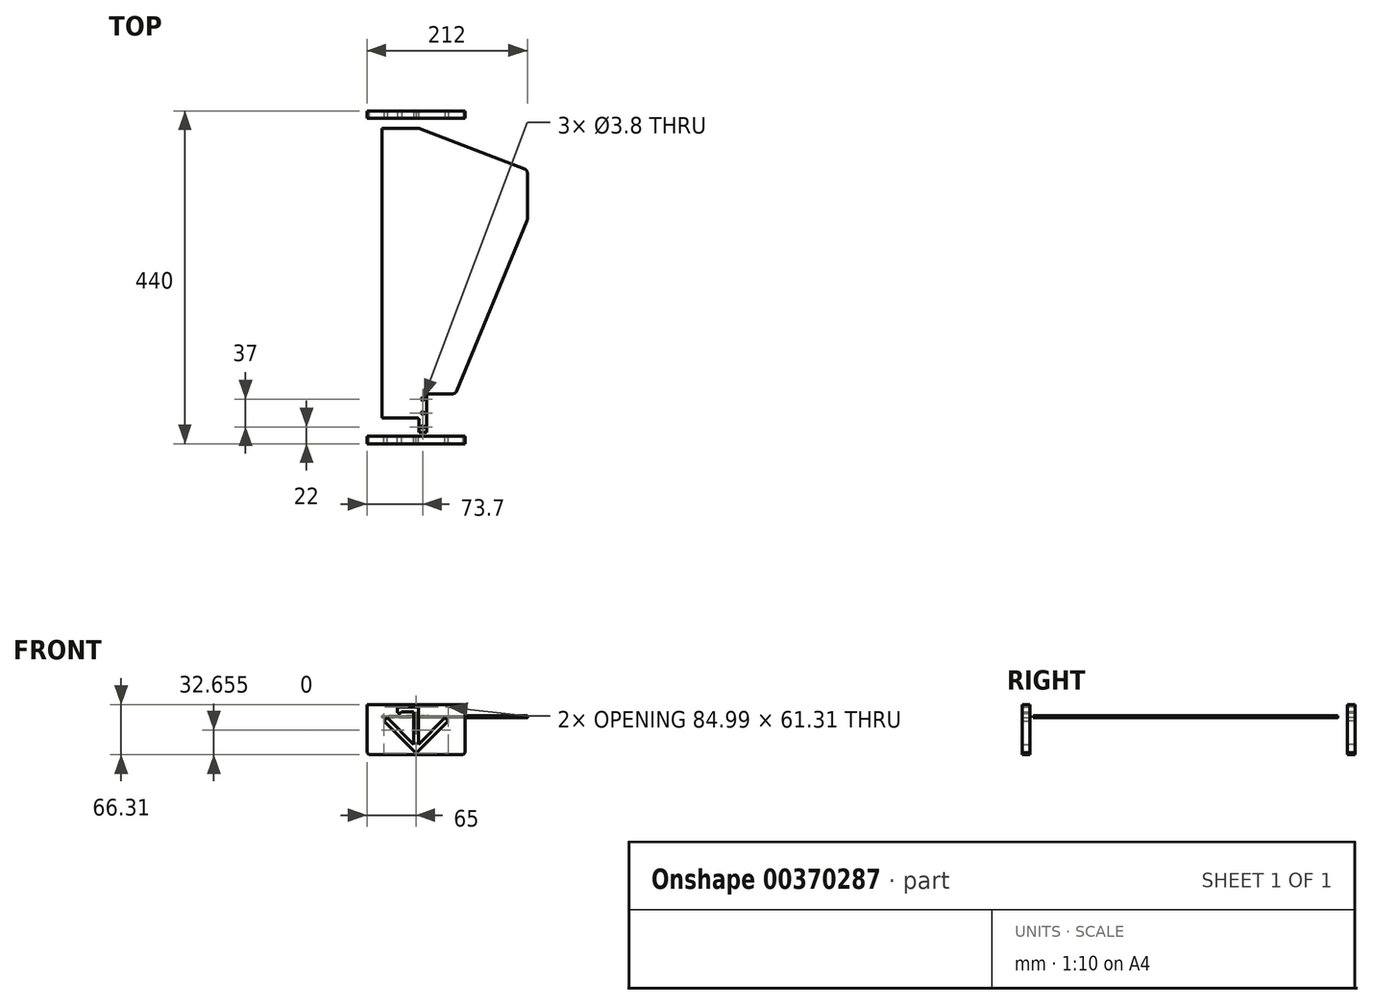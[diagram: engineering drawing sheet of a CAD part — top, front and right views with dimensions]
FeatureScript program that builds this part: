
annotation { "Feature Type Name" : "Feature", "Feature Type Description" : "" }
export const myFeature = defineFeature(function(context is Context, id is Id, definition is map)
    precondition{}
    {
        {
            var Q0;
            Q0=qCreatedBy(makeId("Top.planeOp"),FACE);
            var sketch = newSketch(context, id + "F0", { "sketchPlane" : qUnion([Q0])});
            skLineSegment(sketch, "E0", {"start": v(53.19, 59.09) * mm, "end": v(146.62, 284.65) * mm});
            skLineSegment(sketch, "E1", {"start": v(3.8, 406.67) * mm, "end": v(143.8, 352.93) * mm});
            skLineSegment(sketch, "E2", {"start": v(13.7, 5) * mm, "end": v(13.7, 53) * mm});
            skLineSegment(sketch, "E3", {"start": v(16.7, 56) * mm, "end": v(48.57, 56) * mm});
            skLineSegment(sketch, "E4", {"start": v(4, 5) * mm, "end": v(13.7, 5) * mm});
            skLineSegment(sketch, "E5", {"start": v(147, 348.26) * mm, "end": v(147, 286.57) * mm});
            skArc(sketch, "E6.filletArc", {"start": v(3.8, 406.67) * mm, "mid": v(2.91, 406.92) * mm, "end": v(2, 407) * mm});
            skPoint(sketch, "E7.visualSharp", {"position": v(147, 351.7) * mm});
            skArc(sketch, "E7.filletArc", {"start": v(147, 348.26) * mm, "mid": v(146.12, 351.1) * mm, "end": v(143.8, 352.93) * mm});
            skPoint(sketch, "E8.visualSharp", {"position": v(147, 285.57) * mm});
            skArc(sketch, "E8.filletArc", {"start": v(146.62, 284.65) * mm, "mid": v(146.9, 285.6) * mm, "end": v(147, 286.57) * mm});
            skPoint(sketch, "E9.visualSharp", {"position": v(51.9, 56) * mm});
            skArc(sketch, "E9.filletArc", {"start": v(48.57, 56) * mm, "mid": v(51.35, 56.84) * mm, "end": v(53.19, 59.09) * mm});
            skArc(sketch, "E10.filletArc", {"start": v(16.7, 56) * mm, "mid": v(14.58, 55.12) * mm, "end": v(13.7, 53) * mm});
            skCircle(sketch, "E11", {"center": v(8.7, 12) * mm, "radius": 1.9 * mm});
            skCircle(sketch, "E12", {"center": v(8.7, 49) * mm, "radius": 1.9 * mm});
            skLineSegment(sketch, "E13.0", {"start": v(8.7, 12) * mm, "end": v(8.7, 49) * mm, "construction": true});
            skCircle(sketch, "E14", {"center": v(8.7, 30.5) * mm, "radius": 1.9 * mm});
            skLineSegment(sketch, "E15", {"start": v(2, 407) * mm, "end": v(-45, 407) * mm});
            skLineSegment(sketch, "E16", {"start": v(-45, 407) * mm, "end": v(-45, 24) * mm});
            skLineSegment(sketch, "E17", {"start": v(-45, 24) * mm, "end": v(1, 24) * mm});
            skLineSegment(sketch, "E18", {"start": v(4, 21) * mm, "end": v(4, 5) * mm});
            skPoint(sketch, "E19.visualSharp", {"position": v(4, 24) * mm});
            skArc(sketch, "E19.filletArc", {"start": v(4, 21) * mm, "mid": v(3.12, 23.12) * mm, "end": v(1, 24) * mm});
            skPoint(sketch, "E20", {"position": v(0, 0) * mm});
            skSolve(sketch);
        }
        {
            var Q0;
            Q0=qCreatedBy(makeId("Front.planeOp"),FACE);
            var sketch = newSketch(context, id + "F1", { "sketchPlane" : qUnion([Q0])});
            skPoint(sketch, "E21", {"position": v(-38.18, -3) * mm});
            skLineSegment(sketch, "E22", {"start": v(-65, -51.81) * mm, "end": v(62, -51.81) * mm});
            skLineSegment(sketch, "E23", {"start": v(3.05, -38.13) * mm, "end": v(38.18, -3) * mm});
            skLineSegment(sketch, "E24", {"start": v(38.18, -3) * mm, "end": v(42.5, -7.31) * mm});
            skLineSegment(sketch, "E25", {"start": v(42.5, -7.31) * mm, "end": v(0, -49.81) * mm});
            skLineSegment(sketch, "E26", {"start": v(0, -49.81) * mm, "end": v(-42.5, -7.31) * mm});
            skLineSegment(sketch, "E27", {"start": v(-42.5, -7.31) * mm, "end": v(-38.18, -3) * mm});
            skLineSegment(sketch, "E28", {"start": v(-38.18, -3) * mm, "end": v(-3.05, -38.13) * mm});
            skPoint(sketch, "E29", {"position": v(0, -51.81) * mm});
            skLineSegment(sketch, "E30.direction1", {"start": v(-65, -51.81) * mm, "end": v(0, -51.81) * mm, "construction": true});
            skLineSegment(sketch, "E31", {"start": v(62, -51.81) * mm, "end": v(65, -48.81) * mm});
            skPoint(sketch, "E32.orphan", {"position": v(65, -51.81) * mm});
            skLineSegment(sketch, "E33", {"start": v(-62, -51.81) * mm, "end": v(-65, -48.81) * mm});
            skLineSegment(sketch, "E34", {"start": v(-7.92, 197.19) * mm, "end": v(-41.42, 197.19) * mm});
            skLineSegment(sketch, "E35", {"start": v(-44.42, 194.19) * mm, "end": v(-41.42, 197.19) * mm});
            skLineSegment(sketch, "E36", {"start": v(-7.92, 197.19) * mm, "end": v(-4.92, 194.19) * mm});
            skLineSegment(sketch, "E37", {"start": v(5.5, 194.19) * mm, "end": v(8.5, 197.19) * mm});
            skPoint(sketch, "E38.orphan", {"position": v(-4.92, 197.19) * mm});
            skPoint(sketch, "E39.orphan", {"position": v(6.08, 197.19) * mm});
            skLineSegment(sketch, "E40", {"start": v(-3.05, -38.13) * mm, "end": v(-3.05, 4.5) * mm});
            skLineSegment(sketch, "E41", {"start": v(3.05, -38.13) * mm, "end": v(3.05, 5) * mm});
            skPoint(sketch, "E42", {"position": v(38.18, -3) * mm});
            skPoint(sketch, "E43", {"position": v(38.18, 0) * mm});
            skCircle(sketch, "E44", {"center": v(0, 3) * mm, "radius": 3 * mm});
            skLineSegment(sketch, "E45", {"start": v(-3.55, 5) * mm, "end": v(-19.28, 5) * mm});
            skArc(sketch, "E46", {"start": v(-25.11, 6) * mm, "mid": v(-22.62, 3.04) * mm, "end": v(-19.28, 5) * mm});
            skLineSegment(sketch, "E47", {"start": v(-25.11, 11.5) * mm, "end": v(3.05, 11.5) * mm});
            skLineSegment(sketch, "E48", {"start": v(-25.11, 11.5) * mm, "end": v(-25.11, 6) * mm});
            skLineSegment(sketch, "E49", {"start": v(-3.55, 5) * mm, "end": v(-3.05, 4.5) * mm});
            skLineSegment(sketch, "E50", {"start": v(3.05, 5) * mm, "end": v(3.05, 11.5) * mm});
            skPoint(sketch, "E51.orphan", {"position": v(-3.05, 5) * mm});
            skLineSegment(sketch, "E52", {"start": v(-65, -48.81) * mm, "end": v(-65, 14.5) * mm});
            skLineSegment(sketch, "E53", {"start": v(-65, 14.5) * mm, "end": v(65, 14.5) * mm});
            skLineSegment(sketch, "E54", {"start": v(65, 14.5) * mm, "end": v(65, -48.81) * mm});
            skPoint(sketch, "E55", {"position": v(-29, -7.95) * mm});
            skSolve(sketch);
        }
        {
            var Q0;
            Q0=qSketchRegion(id+"F1",true);
            extrude(context, id + "F2", {"entities" : qUnion([Q0]), "depth" : 10 * mm});
        }
        {
            var Q0;
            Q0=qCreatedBy(makeId("Front.planeOp"),FACE);
            cPlane(context, id + "F3", {"entities" : qUnion([Q0]), "cplaneType" : CPlaneType.OFFSET, "offset" : 210 * mm, "oppositeDirection" : true, "width" : 150 * mm, "height" : 150 * mm});
        }
        {
            var Q0;
            Q0=makeQuery(id+"F2.opExtrude","SWEPT_BODY",BODY,{"disambiguationData":[OSD([sQuery(id+"F1.wireOp",EDGE,"E22"),sQuery(id+"F1.wireOp",EDGE,"1cbbb176-f40a-4f1c-aaf5-e4b3a7756a65"),sQuery(id+"F1.wireOp",EDGE,"0db14ab7-eb58-4049-9c12-30ca4f5b9e90"),sQuery(id+"F1.wireOp",EDGE,"ab1c63a4-a027-4243-88f4-a372497609cb"),sQuery(id+"F1.wireOp",EDGE,"E23"),sQuery(id+"F1.wireOp",EDGE,"E24"),sQuery(id+"F1.wireOp",EDGE,"E25"),sQuery(id+"F1.wireOp",EDGE,"E26"),sQuery(id+"F1.wireOp",EDGE,"E27"),sQuery(id+"F1.wireOp",EDGE,"E28"),sQuery(id+"F1.wireOp",EDGE,"b1abd40f-1537-4efa-8357-bc5ce063cbbe"),sQuery(id+"F1.wireOp",EDGE,"d6b29baa-6176-45ec-b0cb-b8b1ffd4a9fb"),sQuery(id+"F1.wireOp",EDGE,"2be75464-0c29-4c82-b3b4-490e88410c14"),sQuery(id+"F1.wireOp",EDGE,"684266eb-fe4b-4d2b-8d3a-21344d5b1583.0.1.0"),sQuery(id+"F1.wireOp",EDGE,"684266eb-fe4b-4d2b-8d3a-21344d5b1583.0.1.1"),sQuery(id+"F1.wireOp",EDGE,"684266eb-fe4b-4d2b-8d3a-21344d5b1583.0.1.3"),sQuery(id+"F1.wireOp",EDGE,"684266eb-fe4b-4d2b-8d3a-21344d5b1583.0.1.4"),sQuery(id+"F1.wireOp",EDGE,"684266eb-fe4b-4d2b-8d3a-21344d5b1583.0.1.5"),sQuery(id+"F1.wireOp",EDGE,"684266eb-fe4b-4d2b-8d3a-21344d5b1583.0.1.6"),sQuery(id+"F1.wireOp",EDGE,"684266eb-fe4b-4d2b-8d3a-21344d5b1583.0.1.7"),sQuery(id+"F1.wireOp",EDGE,"684266eb-fe4b-4d2b-8d3a-21344d5b1583.0.1.9"),sQuery(id+"F1.wireOp",EDGE,"684266eb-fe4b-4d2b-8d3a-21344d5b1583.0.1.10"),sQuery(id+"F1.wireOp",EDGE,"684266eb-fe4b-4d2b-8d3a-21344d5b1583.0.1.11"),sQuery(id+"F1.wireOp",EDGE,"684266eb-fe4b-4d2b-8d3a-21344d5b1583.0.1.12"),sQuery(id+"F1.wireOp",EDGE,"684266eb-fe4b-4d2b-8d3a-21344d5b1583.0.2.0"),sQuery(id+"F1.wireOp",EDGE,"684266eb-fe4b-4d2b-8d3a-21344d5b1583.0.2.1"),sQuery(id+"F1.wireOp",EDGE,"684266eb-fe4b-4d2b-8d3a-21344d5b1583.0.2.3"),sQuery(id+"F1.wireOp",EDGE,"684266eb-fe4b-4d2b-8d3a-21344d5b1583.0.2.4"),sQuery(id+"F1.wireOp",EDGE,"684266eb-fe4b-4d2b-8d3a-21344d5b1583.0.2.5"),sQuery(id+"F1.wireOp",EDGE,"684266eb-fe4b-4d2b-8d3a-21344d5b1583.0.2.6"),sQuery(id+"F1.wireOp",EDGE,"684266eb-fe4b-4d2b-8d3a-21344d5b1583.0.2.7"),sQuery(id+"F1.wireOp",EDGE,"684266eb-fe4b-4d2b-8d3a-21344d5b1583.0.2.9"),sQuery(id+"F1.wireOp",EDGE,"684266eb-fe4b-4d2b-8d3a-21344d5b1583.0.2.10"),sQuery(id+"F1.wireOp",EDGE,"684266eb-fe4b-4d2b-8d3a-21344d5b1583.0.2.11"),sQuery(id+"F1.wireOp",EDGE,"684266eb-fe4b-4d2b-8d3a-21344d5b1583.0.2.12"),sQuery(id+"F1.wireOp",EDGE,"684266eb-fe4b-4d2b-8d3a-21344d5b1583.0.3.0"),sQuery(id+"F1.wireOp",EDGE,"684266eb-fe4b-4d2b-8d3a-21344d5b1583.0.3.1"),sQuery(id+"F1.wireOp",EDGE,"684266eb-fe4b-4d2b-8d3a-21344d5b1583.0.3.3"),sQuery(id+"F1.wireOp",EDGE,"684266eb-fe4b-4d2b-8d3a-21344d5b1583.0.3.4"),sQuery(id+"F1.wireOp",EDGE,"684266eb-fe4b-4d2b-8d3a-21344d5b1583.0.3.5"),sQuery(id+"F1.wireOp",EDGE,"684266eb-fe4b-4d2b-8d3a-21344d5b1583.0.3.6"),sQuery(id+"F1.wireOp",EDGE,"684266eb-fe4b-4d2b-8d3a-21344d5b1583.0.3.7"),sQuery(id+"F1.wireOp",EDGE,"684266eb-fe4b-4d2b-8d3a-21344d5b1583.0.3.9"),sQuery(id+"F1.wireOp",EDGE,"684266eb-fe4b-4d2b-8d3a-21344d5b1583.0.3.10"),sQuery(id+"F1.wireOp",EDGE,"684266eb-fe4b-4d2b-8d3a-21344d5b1583.0.3.11"),sQuery(id+"F1.wireOp",EDGE,"684266eb-fe4b-4d2b-8d3a-21344d5b1583.0.3.12"),sQuery(id+"F1.wireOp",EDGE,"684266eb-fe4b-4d2b-8d3a-21344d5b1583.0.4.0"),sQuery(id+"F1.wireOp",EDGE,"684266eb-fe4b-4d2b-8d3a-21344d5b1583.0.4.1"),sQuery(id+"F1.wireOp",EDGE,"684266eb-fe4b-4d2b-8d3a-21344d5b1583.0.4.3"),sQuery(id+"F1.wireOp",EDGE,"684266eb-fe4b-4d2b-8d3a-21344d5b1583.0.4.4"),sQuery(id+"F1.wireOp",EDGE,"684266eb-fe4b-4d2b-8d3a-21344d5b1583.0.4.5"),sQuery(id+"F1.wireOp",EDGE,"684266eb-fe4b-4d2b-8d3a-21344d5b1583.0.4.6"),sQuery(id+"F1.wireOp",EDGE,"684266eb-fe4b-4d2b-8d3a-21344d5b1583.0.4.7"),sQuery(id+"F1.wireOp",EDGE,"684266eb-fe4b-4d2b-8d3a-21344d5b1583.0.4.9"),sQuery(id+"F1.wireOp",EDGE,"684266eb-fe4b-4d2b-8d3a-21344d5b1583.0.4.10"),sQuery(id+"F1.wireOp",EDGE,"684266eb-fe4b-4d2b-8d3a-21344d5b1583.0.4.11"),sQuery(id+"F1.wireOp",EDGE,"684266eb-fe4b-4d2b-8d3a-21344d5b1583.0.4.12"),sQuery(id+"F1.wireOp",EDGE,"684266eb-fe4b-4d2b-8d3a-21344d5b1583.0.5.0"),sQuery(id+"F1.wireOp",EDGE,"684266eb-fe4b-4d2b-8d3a-21344d5b1583.0.5.1"),sQuery(id+"F1.wireOp",EDGE,"684266eb-fe4b-4d2b-8d3a-21344d5b1583.0.5.3"),sQuery(id+"F1.wireOp",EDGE,"684266eb-fe4b-4d2b-8d3a-21344d5b1583.0.5.4"),sQuery(id+"F1.wireOp",EDGE,"684266eb-fe4b-4d2b-8d3a-21344d5b1583.0.5.5"),sQuery(id+"F1.wireOp",EDGE,"684266eb-fe4b-4d2b-8d3a-21344d5b1583.0.5.6"),sQuery(id+"F1.wireOp",EDGE,"684266eb-fe4b-4d2b-8d3a-21344d5b1583.0.5.7"),sQuery(id+"F1.wireOp",EDGE,"684266eb-fe4b-4d2b-8d3a-21344d5b1583.0.5.9"),sQuery(id+"F1.wireOp",EDGE,"684266eb-fe4b-4d2b-8d3a-21344d5b1583.0.5.10"),sQuery(id+"F1.wireOp",EDGE,"684266eb-fe4b-4d2b-8d3a-21344d5b1583.0.5.11"),sQuery(id+"F1.wireOp",EDGE,"684266eb-fe4b-4d2b-8d3a-21344d5b1583.0.5.12"),sQuery(id+"F1.wireOp",EDGE,"684266eb-fe4b-4d2b-8d3a-21344d5b1583.0.6.0"),sQuery(id+"F1.wireOp",EDGE,"684266eb-fe4b-4d2b-8d3a-21344d5b1583.0.6.1"),sQuery(id+"F1.wireOp",EDGE,"684266eb-fe4b-4d2b-8d3a-21344d5b1583.0.6.3"),sQuery(id+"F1.wireOp",EDGE,"684266eb-fe4b-4d2b-8d3a-21344d5b1583.0.6.4"),sQuery(id+"F1.wireOp",EDGE,"684266eb-fe4b-4d2b-8d3a-21344d5b1583.0.6.5"),sQuery(id+"F1.wireOp",EDGE,"684266eb-fe4b-4d2b-8d3a-21344d5b1583.0.6.6"),sQuery(id+"F1.wireOp",EDGE,"684266eb-fe4b-4d2b-8d3a-21344d5b1583.0.6.7"),sQuery(id+"F1.wireOp",EDGE,"684266eb-fe4b-4d2b-8d3a-21344d5b1583.0.6.9"),sQuery(id+"F1.wireOp",EDGE,"684266eb-fe4b-4d2b-8d3a-21344d5b1583.0.6.10"),sQuery(id+"F1.wireOp",EDGE,"684266eb-fe4b-4d2b-8d3a-21344d5b1583.0.6.11"),sQuery(id+"F1.wireOp",EDGE,"684266eb-fe4b-4d2b-8d3a-21344d5b1583.0.6.12"),sQuery(id+"F1.wireOp",EDGE,"684266eb-fe4b-4d2b-8d3a-21344d5b1583.0.7.0"),sQuery(id+"F1.wireOp",EDGE,"684266eb-fe4b-4d2b-8d3a-21344d5b1583.0.7.1"),sQuery(id+"F1.wireOp",EDGE,"684266eb-fe4b-4d2b-8d3a-21344d5b1583.0.7.3"),sQuery(id+"F1.wireOp",EDGE,"684266eb-fe4b-4d2b-8d3a-21344d5b1583.0.7.4"),sQuery(id+"F1.wireOp",EDGE,"684266eb-fe4b-4d2b-8d3a-21344d5b1583.0.7.5"),sQuery(id+"F1.wireOp",EDGE,"684266eb-fe4b-4d2b-8d3a-21344d5b1583.0.7.6"),sQuery(id+"F1.wireOp",EDGE,"684266eb-fe4b-4d2b-8d3a-21344d5b1583.0.7.7"),sQuery(id+"F1.wireOp",EDGE,"684266eb-fe4b-4d2b-8d3a-21344d5b1583.0.7.9"),sQuery(id+"F1.wireOp",EDGE,"684266eb-fe4b-4d2b-8d3a-21344d5b1583.0.7.10"),sQuery(id+"F1.wireOp",EDGE,"684266eb-fe4b-4d2b-8d3a-21344d5b1583.0.7.11"),sQuery(id+"F1.wireOp",EDGE,"684266eb-fe4b-4d2b-8d3a-21344d5b1583.0.7.12"),sQuery(id+"F1.wireOp",EDGE,"5e48dbf6-bd7d-4e66-b090-3bfb0b5fe9680.MirrorCS"),sQuery(id+"F1.wireOp",EDGE,"5e48dbf6-bd7d-4e66-b090-3bfb0b5fe9681.MirrorCS"),sQuery(id+"F1.wireOp",EDGE,"5e48dbf6-bd7d-4e66-b090-3bfb0b5fe9682.MirrorCS"),sQuery(id+"F1.wireOp",EDGE,"5e48dbf6-bd7d-4e66-b090-3bfb0b5fe9683.MirrorCS"),sQuery(id+"F1.wireOp",EDGE,"5e48dbf6-bd7d-4e66-b090-3bfb0b5fe9684.MirrorCS"),sQuery(id+"F1.wireOp",EDGE,"5e48dbf6-bd7d-4e66-b090-3bfb0b5fe9685.MirrorCS"),sQuery(id+"F1.wireOp",EDGE,"5e48dbf6-bd7d-4e66-b090-3bfb0b5fe9686.MirrorCS"),sQuery(id+"F1.wireOp",EDGE,"5e48dbf6-bd7d-4e66-b090-3bfb0b5fe9687.MirrorCS"),sQuery(id+"F1.wireOp",EDGE,"5e48dbf6-bd7d-4e66-b090-3bfb0b5fe9688.MirrorCS"),sQuery(id+"F1.wireOp",EDGE,"5e48dbf6-bd7d-4e66-b090-3bfb0b5fe9689.MirrorCS"),sQuery(id+"F1.wireOp",EDGE,"5e48dbf6-bd7d-4e66-b090-3bfb0b5fe96810.MirrorCS"),sQuery(id+"F1.wireOp",EDGE,"5e48dbf6-bd7d-4e66-b090-3bfb0b5fe96811.MirrorCS"),sQuery(id+"F1.wireOp",EDGE,"5e48dbf6-bd7d-4e66-b090-3bfb0b5fe96812.MirrorCS"),sQuery(id+"F1.wireOp",EDGE,"5e48dbf6-bd7d-4e66-b090-3bfb0b5fe96813.MirrorCS"),sQuery(id+"F1.wireOp",EDGE,"5e48dbf6-bd7d-4e66-b090-3bfb0b5fe96814.MirrorCS"),sQuery(id+"F1.wireOp",EDGE,"5e48dbf6-bd7d-4e66-b090-3bfb0b5fe96815.MirrorCS"),sQuery(id+"F1.wireOp",EDGE,"5e48dbf6-bd7d-4e66-b090-3bfb0b5fe96816.MirrorCS"),sQuery(id+"F1.wireOp",EDGE,"5e48dbf6-bd7d-4e66-b090-3bfb0b5fe96817.MirrorCS"),sQuery(id+"F1.wireOp",EDGE,"5e48dbf6-bd7d-4e66-b090-3bfb0b5fe96818.MirrorCS"),sQuery(id+"F1.wireOp",EDGE,"5e48dbf6-bd7d-4e66-b090-3bfb0b5fe96819.MirrorCS"),sQuery(id+"F1.wireOp",EDGE,"5e48dbf6-bd7d-4e66-b090-3bfb0b5fe96820.MirrorCS"),sQuery(id+"F1.wireOp",EDGE,"5e48dbf6-bd7d-4e66-b090-3bfb0b5fe96821.MirrorCS"),sQuery(id+"F1.wireOp",EDGE,"5e48dbf6-bd7d-4e66-b090-3bfb0b5fe96822.MirrorCS"),sQuery(id+"F1.wireOp",EDGE,"5e48dbf6-bd7d-4e66-b090-3bfb0b5fe96823.MirrorCS"),sQuery(id+"F1.wireOp",EDGE,"5e48dbf6-bd7d-4e66-b090-3bfb0b5fe96824.MirrorCS"),sQuery(id+"F1.wireOp",EDGE,"5e48dbf6-bd7d-4e66-b090-3bfb0b5fe96825.MirrorCS"),sQuery(id+"F1.wireOp",EDGE,"5e48dbf6-bd7d-4e66-b090-3bfb0b5fe96826.MirrorCS"),sQuery(id+"F1.wireOp",EDGE,"5e48dbf6-bd7d-4e66-b090-3bfb0b5fe96827.MirrorCS"),sQuery(id+"F1.wireOp",EDGE,"5e48dbf6-bd7d-4e66-b090-3bfb0b5fe96828.MirrorCS"),sQuery(id+"F1.wireOp",EDGE,"5e48dbf6-bd7d-4e66-b090-3bfb0b5fe96829.MirrorCS"),sQuery(id+"F1.wireOp",EDGE,"5e48dbf6-bd7d-4e66-b090-3bfb0b5fe96830.MirrorCS"),sQuery(id+"F1.wireOp",EDGE,"5e48dbf6-bd7d-4e66-b090-3bfb0b5fe96831.MirrorCS"),sQuery(id+"F1.wireOp",EDGE,"5e48dbf6-bd7d-4e66-b090-3bfb0b5fe96832.MirrorCS"),sQuery(id+"F1.wireOp",EDGE,"5e48dbf6-bd7d-4e66-b090-3bfb0b5fe96833.MirrorCS"),sQuery(id+"F1.wireOp",EDGE,"5e48dbf6-bd7d-4e66-b090-3bfb0b5fe96834.MirrorCS"),sQuery(id+"F1.wireOp",EDGE,"5e48dbf6-bd7d-4e66-b090-3bfb0b5fe96835.MirrorCS"),sQuery(id+"F1.wireOp",EDGE,"5e48dbf6-bd7d-4e66-b090-3bfb0b5fe96836.MirrorCS"),sQuery(id+"F1.wireOp",EDGE,"5e48dbf6-bd7d-4e66-b090-3bfb0b5fe96837.MirrorCS"),sQuery(id+"F1.wireOp",EDGE,"5e48dbf6-bd7d-4e66-b090-3bfb0b5fe96838.MirrorCS"),sQuery(id+"F1.wireOp",EDGE,"5e48dbf6-bd7d-4e66-b090-3bfb0b5fe96839.MirrorCS"),sQuery(id+"F1.wireOp",EDGE,"5e48dbf6-bd7d-4e66-b090-3bfb0b5fe96840.MirrorCS"),sQuery(id+"F1.wireOp",EDGE,"5e48dbf6-bd7d-4e66-b090-3bfb0b5fe96841.MirrorCS"),sQuery(id+"F1.wireOp",EDGE,"5e48dbf6-bd7d-4e66-b090-3bfb0b5fe96842.MirrorCS"),sQuery(id+"F1.wireOp",EDGE,"5e48dbf6-bd7d-4e66-b090-3bfb0b5fe96843.MirrorCS"),sQuery(id+"F1.wireOp",EDGE,"5e48dbf6-bd7d-4e66-b090-3bfb0b5fe96844.MirrorCS"),sQuery(id+"F1.wireOp",EDGE,"5e48dbf6-bd7d-4e66-b090-3bfb0b5fe96846.MirrorCS"),sQuery(id+"F1.wireOp",EDGE,"5e48dbf6-bd7d-4e66-b090-3bfb0b5fe96847.MirrorCS"),sQuery(id+"F1.wireOp",EDGE,"5e48dbf6-bd7d-4e66-b090-3bfb0b5fe96848.MirrorCS"),sQuery(id+"F1.wireOp",EDGE,"5e48dbf6-bd7d-4e66-b090-3bfb0b5fe96849.MirrorCS"),sQuery(id+"F1.wireOp",EDGE,"5e48dbf6-bd7d-4e66-b090-3bfb0b5fe96850.MirrorCS"),sQuery(id+"F1.wireOp",EDGE,"5e48dbf6-bd7d-4e66-b090-3bfb0b5fe96851.MirrorCS"),sQuery(id+"F1.wireOp",EDGE,"5e48dbf6-bd7d-4e66-b090-3bfb0b5fe96852.MirrorCS"),sQuery(id+"F1.wireOp",EDGE,"5e48dbf6-bd7d-4e66-b090-3bfb0b5fe96853.MirrorCS"),sQuery(id+"F1.wireOp",EDGE,"5e48dbf6-bd7d-4e66-b090-3bfb0b5fe96854.MirrorCS"),sQuery(id+"F1.wireOp",EDGE,"5e48dbf6-bd7d-4e66-b090-3bfb0b5fe96855.MirrorCS"),sQuery(id+"F1.wireOp",EDGE,"5e48dbf6-bd7d-4e66-b090-3bfb0b5fe96856.MirrorCS"),sQuery(id+"F1.wireOp",EDGE,"5e48dbf6-bd7d-4e66-b090-3bfb0b5fe96857.MirrorCS"),sQuery(id+"F1.wireOp",EDGE,"5e48dbf6-bd7d-4e66-b090-3bfb0b5fe96858.MirrorCS"),sQuery(id+"F1.wireOp",EDGE,"5e48dbf6-bd7d-4e66-b090-3bfb0b5fe96859.MirrorCS"),sQuery(id+"F1.wireOp",EDGE,"5e48dbf6-bd7d-4e66-b090-3bfb0b5fe96860.MirrorCS"),sQuery(id+"F1.wireOp",EDGE,"5e48dbf6-bd7d-4e66-b090-3bfb0b5fe96861.MirrorCS"),sQuery(id+"F1.wireOp",EDGE,"5e48dbf6-bd7d-4e66-b090-3bfb0b5fe96862.MirrorCS"),sQuery(id+"F1.wireOp",EDGE,"5e48dbf6-bd7d-4e66-b090-3bfb0b5fe96863.MirrorCS"),sQuery(id+"F1.wireOp",EDGE,"5e48dbf6-bd7d-4e66-b090-3bfb0b5fe96864.MirrorCS"),sQuery(id+"F1.wireOp",EDGE,"5e48dbf6-bd7d-4e66-b090-3bfb0b5fe96865.MirrorCS"),sQuery(id+"F1.wireOp",EDGE,"5e48dbf6-bd7d-4e66-b090-3bfb0b5fe96866.MirrorCS"),sQuery(id+"F1.wireOp",EDGE,"5e48dbf6-bd7d-4e66-b090-3bfb0b5fe96867.MirrorCS"),sQuery(id+"F1.wireOp",EDGE,"5e48dbf6-bd7d-4e66-b090-3bfb0b5fe96868.MirrorCS"),sQuery(id+"F1.wireOp",EDGE,"5e48dbf6-bd7d-4e66-b090-3bfb0b5fe96869.MirrorCS"),sQuery(id+"F1.wireOp",EDGE,"5e48dbf6-bd7d-4e66-b090-3bfb0b5fe96870.MirrorCS"),sQuery(id+"F1.wireOp",EDGE,"5e48dbf6-bd7d-4e66-b090-3bfb0b5fe96871.MirrorCS"),sQuery(id+"F1.wireOp",EDGE,"5e48dbf6-bd7d-4e66-b090-3bfb0b5fe96872.MirrorCS"),sQuery(id+"F1.wireOp",EDGE,"5e48dbf6-bd7d-4e66-b090-3bfb0b5fe96875.MirrorCS"),sQuery(id+"F1.wireOp",EDGE,"5e48dbf6-bd7d-4e66-b090-3bfb0b5fe96877.MirrorCS"),sQuery(id+"F1.wireOp",EDGE,"5e48dbf6-bd7d-4e66-b090-3bfb0b5fe96878.MirrorCS"),sQuery(id+"F1.wireOp",EDGE,"5e48dbf6-bd7d-4e66-b090-3bfb0b5fe96880.MirrorCS"),sQuery(id+"F1.wireOp",EDGE,"5e48dbf6-bd7d-4e66-b090-3bfb0b5fe96882.MirrorCS"),sQuery(id+"F1.wireOp",EDGE,"5e48dbf6-bd7d-4e66-b090-3bfb0b5fe96883.MirrorCS"),sQuery(id+"F1.wireOp",EDGE,"5e48dbf6-bd7d-4e66-b090-3bfb0b5fe96886.MirrorCS"),sQuery(id+"F1.wireOp",EDGE,"5e48dbf6-bd7d-4e66-b090-3bfb0b5fe96888.MirrorCS"),sQuery(id+"F1.wireOp",EDGE,"5e48dbf6-bd7d-4e66-b090-3bfb0b5fe96890.MirrorCS"),sQuery(id+"F1.wireOp",EDGE,"5e48dbf6-bd7d-4e66-b090-3bfb0b5fe96892.MirrorCS"),sQuery(id+"F1.wireOp",EDGE,"5e48dbf6-bd7d-4e66-b090-3bfb0b5fe96895.MirrorCS"),sQuery(id+"F1.wireOp",EDGE,"5e48dbf6-bd7d-4e66-b090-3bfb0b5fe96897.MirrorCS"),sQuery(id+"F1.wireOp",EDGE,"5e48dbf6-bd7d-4e66-b090-3bfb0b5fe968101.MirrorCS"),sQuery(id+"F1.wireOp",EDGE,"5e48dbf6-bd7d-4e66-b090-3bfb0b5fe968102.MirrorCS"),sQuery(id+"F1.wireOp",EDGE,"5e48dbf6-bd7d-4e66-b090-3bfb0b5fe968104.MirrorCS"),sQuery(id+"F1.wireOp",EDGE,"5e48dbf6-bd7d-4e66-b090-3bfb0b5fe968106.MirrorCS"),sQuery(id+"F1.wireOp",EDGE,"5e48dbf6-bd7d-4e66-b090-3bfb0b5fe968109.MirrorCS"),sQuery(id+"F1.wireOp",EDGE,"ek9GhSJZ-eJl4-twK5-TzIv-mKVH3UdkhTqk"),sQuery(id+"F1.wireOp",EDGE,"21isNEuG-rZuh-QLDD-1XWf-fwm70vtYFsN0"),sQuery(id+"F1.wireOp",EDGE,"01unO0Bz-F3pu-LKa0-yoft-ag0aoVEs0A1s")])]});
            var Q1;
            Q1=qCreatedBy(id+"F3.planeOp",FACE);
            mirror(context, id + "F4", {"entities" : qUnion([Q0]), "mirrorPlane" : qUnion([Q1])});
        }
        {
            var Q0;
            Q0 = qSketchRegion(id + "F0", true);
            extrude(context, id + "F5", {"entities" : qUnion([Q0]), "oppositeDirection" : true, "depth" : 3 * mm});
        }
    });
